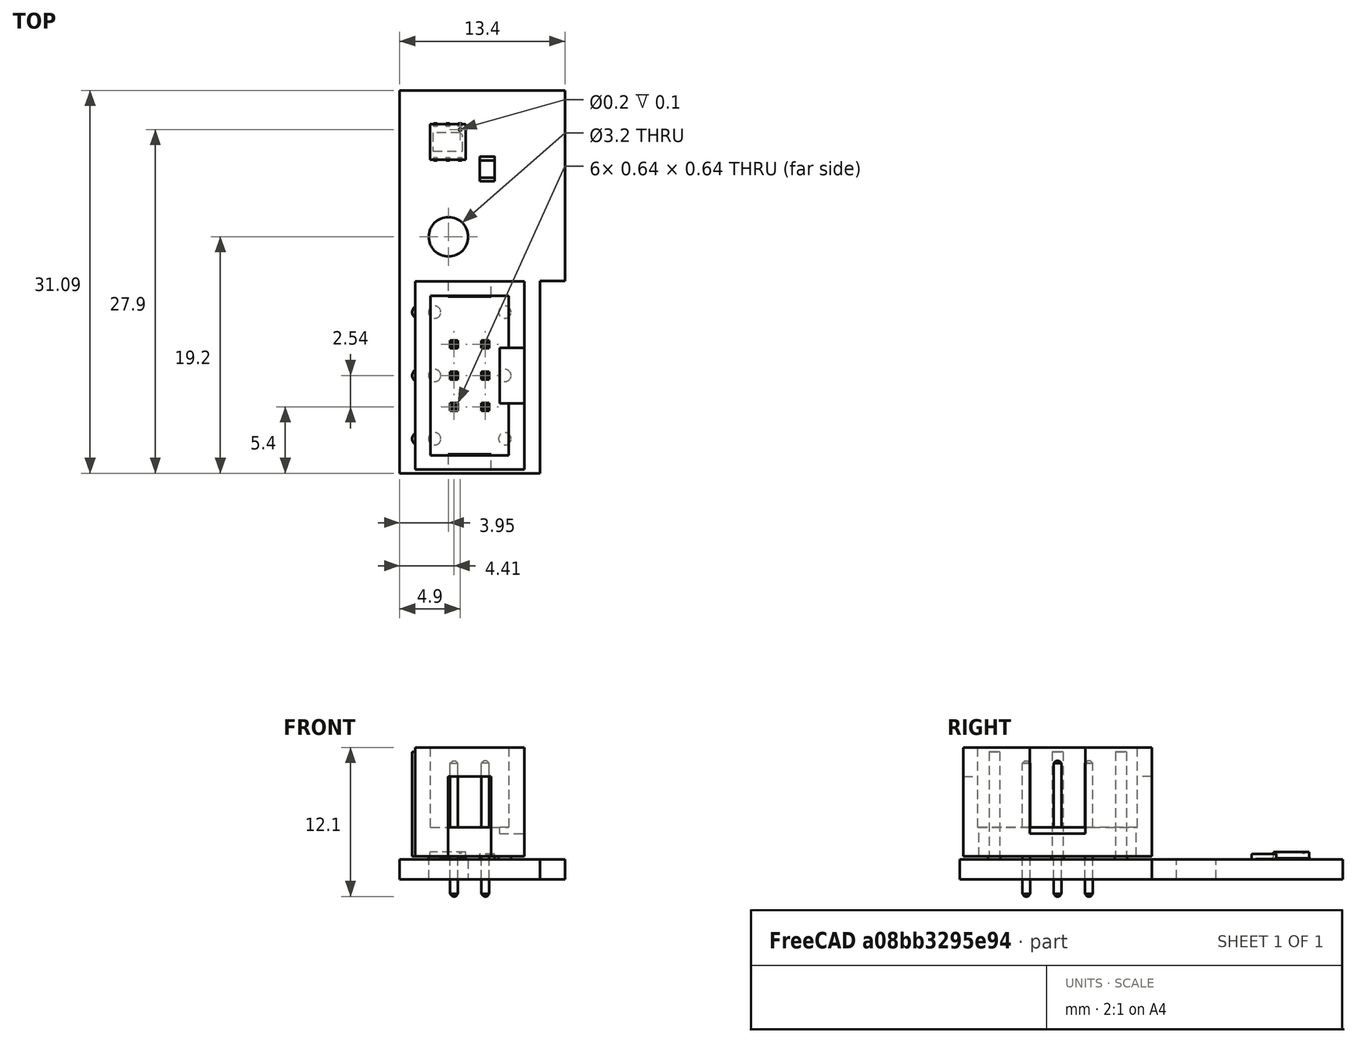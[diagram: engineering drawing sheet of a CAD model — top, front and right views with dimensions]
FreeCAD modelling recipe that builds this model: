
FCSTD DOCUMENT  (FreeCAD 0.19R24291 (Git))
Label: feederFloorPCB
License: All rights reserved
LicenseURL: http://en.wikipedia.org/wiki/All_rights_reserved
objects: Part::Feature×4, App::Part×4, PartDesign::CoordinateSystem×1, Sketcher::SketchObject×1, App::Link×1
note: 6 computed .brp shape members not serialized (recipe doc carries the construction recipe); baked Part::Feature solids carry a one-line shape summary decoded from their .brp

FEATURE [PartDesign::CoordinateSystem] Local_CS_a7f7
  AttacherType = Attacher::AttachEngine3D
FEATURE [Part::Feature] Pcb_a7f7
  shape: bbox 13.4 x 31.09 x 1.6 mm, 10 faces (baked)
FEATURE [Sketcher::SketchObject] PCB_Sketch_a7f7
  FullyConstrained = false
  sketch-geometry (7):
    g0: LineSegment StartX=32.6501 StartY=-40.6 StartZ=0 EndX=32.65 EndY=-56.2 EndZ=0
    g1: LineSegment StartX=34.6501 StartY=-25.1137 StartZ=0 EndX=34.6501 EndY=-40.6 EndZ=0
    g2: LineSegment StartX=29.6501 StartY=-25.1137 StartZ=0 EndX=21.2501 EndY=-25.1137 EndZ=0
    g3: LineSegment StartX=32.6501 StartY=-40.6 StartZ=0 EndX=34.6501 EndY=-40.6 EndZ=0
    g4: LineSegment StartX=29.6501 StartY=-25.1137 StartZ=0 EndX=34.6501 EndY=-25.1137 EndZ=0
    g5: LineSegment StartX=21.25 StartY=-56.2 StartZ=0 EndX=21.2501 EndY=-25.1137 EndZ=0
    g6: LineSegment StartX=32.65 StartY=-56.2 StartZ=0 EndX=21.25 EndY=-56.2 EndZ=0
  constraints (7):
    c: Coincident(g6,g5)
    c: Coincident(g2,g5)
    c: Coincident(g2,g4)
    c: Coincident(g6,g0)
    c: Coincident(g0,g3)
    c: Coincident(g1,g3)
    c: Coincident(g4,g1)
FEATURE [App::Part] Board_Geoms_a7f7
  Group = -> [Local_CS_a7f7,Pcb_a7f7,PCB_Sketch_a7f7]
  Origin = -> Origin
FEATURE [Part::Feature] Shape  label="J1_IDC_Header_2x03_P254mm_Vertical_00005ff989fe"
  Placement = pos=(28.2,-50.8,0) rot=(0,0,1;3.14159rad)
  shape: bbox 9.1 x 15.28 x 12.1 mm, 150 faces (baked)
FEATURE [Part::Feature] Shape001  label="U1_DFN_6_1EP_3x3mm_P1mm_EP15x24mm_3298b6a5c1f5"
  Placement = pos=(25.15,-29.3,0) rot=(0,0,-1;1.5708rad)
  shape: bbox 2.9 x 3 x 0.6 mm, 50 faces (baked)
FEATURE [Part::Feature] Shape002  label="R1_R_0805_2012Metric_87ce4d417120"
  Placement = pos=(28.35,-31.5,0) rot=(0,0,1;1.5708rad)
  shape: bbox 1.2 x 2 x 0.45 mm, 26 faces (baked)
FEATURE [App::Link] R1_R_0805_2012Metric_87ce4d417120_ln_  label="R2_R_0805_2012Metric_acaf19551d1a"
  LinkPlacement = pos=(28.35,-28,0) rot=(0,0,-1;1.5708rad)
  LinkedObject = -> Shape002
  Placement = pos=(28.35,-28,0) rot=(0,0,-1;1.5708rad)
FEATURE [App::Part] Top_a7f7
  Group = -> [Shape,Shape001,Shape002,R1_R_0805_2012Metric_87ce4d417120_ln_]
  Origin = -> Origin003
FEATURE [App::Part] Step_Models_a7f7
  Group = -> [Top_a7f7]
  Origin = -> Origin002
FEATURE [App::Part] Board_a7f7  label="feederFloor"
  Group = -> [Board_Geoms_a7f7,Step_Models_a7f7]
  Origin = -> Origin001
